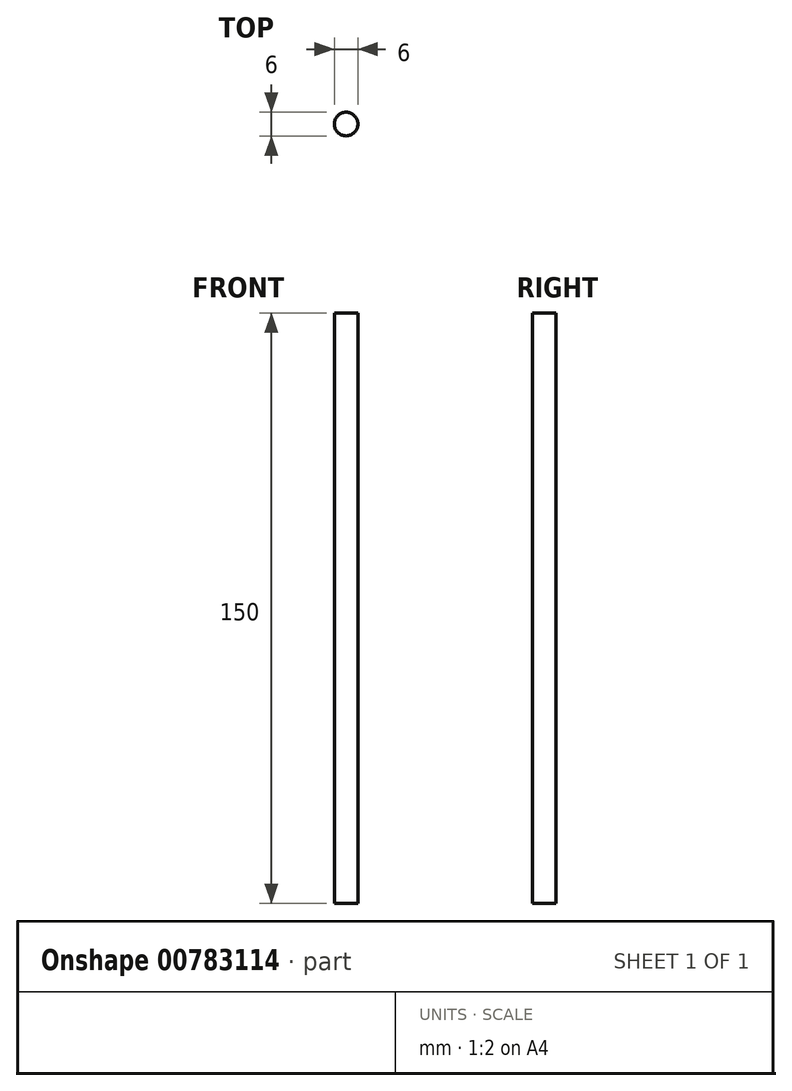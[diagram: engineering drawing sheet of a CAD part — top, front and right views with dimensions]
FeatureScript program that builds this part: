
annotation { "Feature Type Name" : "Feature", "Feature Type Description" : "" }
export const myFeature = defineFeature(function(context is Context, id is Id, definition is map)
    precondition{}
    {
        {
            var Q0;
            Q0=qCreatedBy(makeId("Top.planeOp"),FACE);
            var sketch = newSketch(context, id + "F0", { "sketchPlane" : qUnion([Q0])});
            skCircle(sketch, "E0", {"center": v(0, 0) * mm, "radius": 3 * mm});
            skSolve(sketch);
        }
        {
            var Q0;
            Q0=makeQuery(id+"F0.imprint","IMPRINT",FACE,{"disambiguationData":[TD([[makeQuery(id+"F0.imprint","IMPRINT",EDGE,{"derivedFrom":sQuery(id+"F0.wireOp",EDGE,"E0")}),1.0]])]});
            extrude(context, id + "F1", {"entities" : qUnion([Q0]), "depth" : 150 * mm, "offsetDistance" : 25 * mm});
        }
    });
